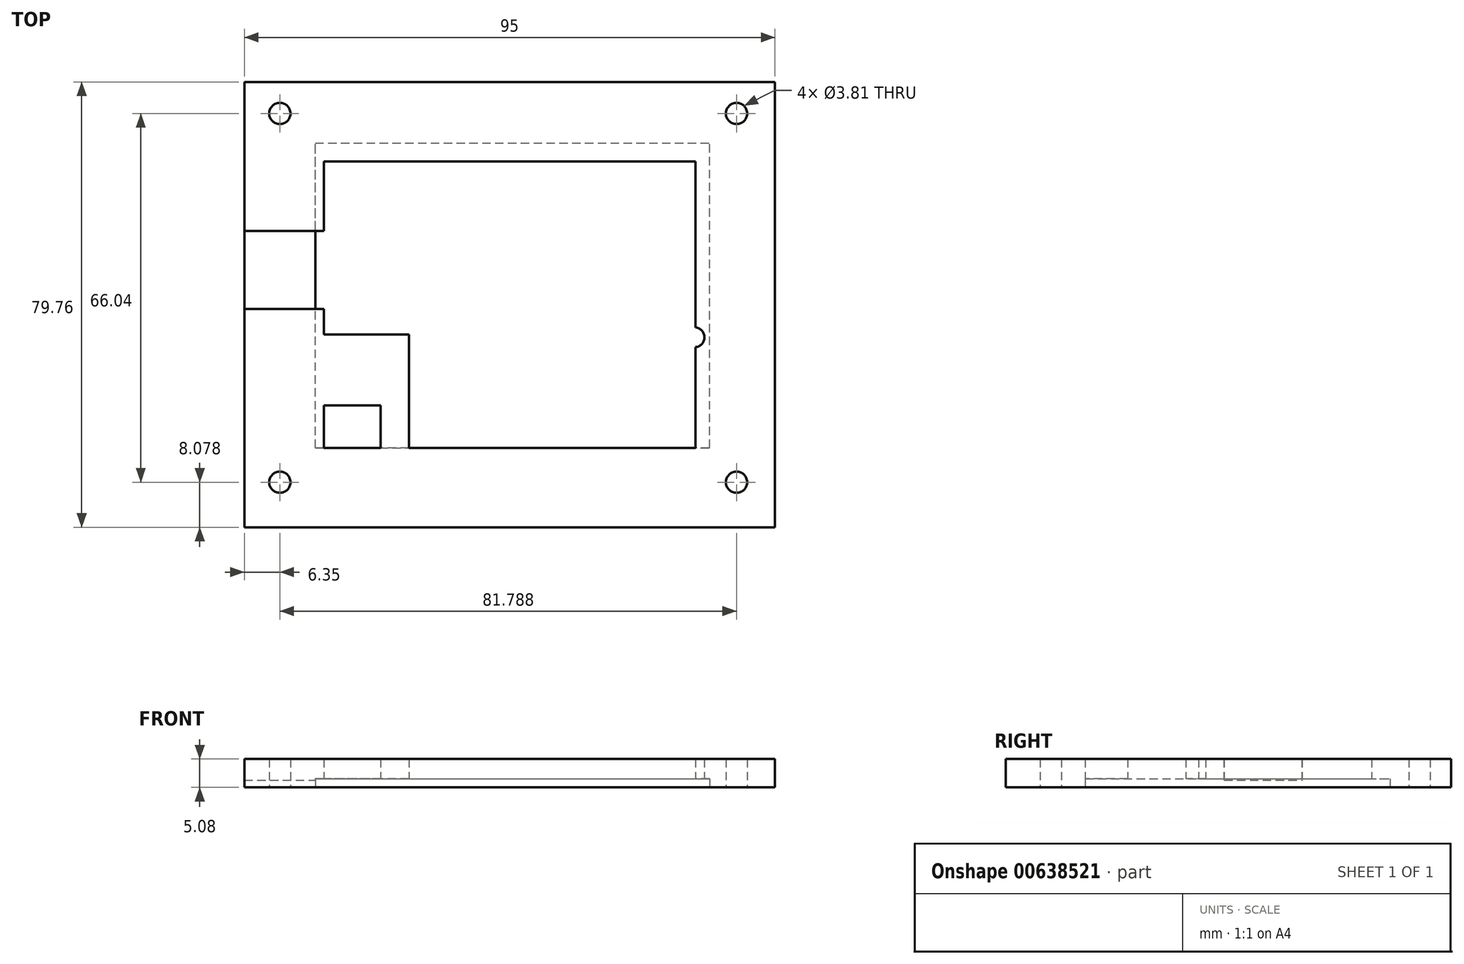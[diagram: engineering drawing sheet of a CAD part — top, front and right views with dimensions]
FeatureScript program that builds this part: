
annotation { "Feature Type Name" : "Feature", "Feature Type Description" : "" }
export const myFeature = defineFeature(function(context is Context, id is Id, definition is map)
    precondition{}
    {
        {
            var Q0;
            Q0=qCreatedBy(makeId("Top.planeOp"),FACE);
            var sketch = newSketch(context, id + "F0", { "sketchPlane" : qUnion([Q0])});
            skLineSegment(sketch, "E0.bottom", {"start": v(0, 0) * mm, "end": v(95, 0) * mm});
            skLineSegment(sketch, "E0.top", {"start": v(0, 79.76) * mm, "end": v(95, 79.76) * mm});
            skLineSegment(sketch, "E0.left", {"start": v(0, 0) * mm, "end": v(0, 79.76) * mm});
            skLineSegment(sketch, "E0.right", {"start": v(95, 0) * mm, "end": v(95, 79.76) * mm});
            skLineSegment(sketch, "E1.bottom", {"start": v(80.77, 65.53) * mm, "end": v(14.22, 65.53) * mm});
            skLineSegment(sketch, "E1.top", {"start": v(80.77, 14.22) * mm, "end": v(29.46, 14.22) * mm});
            skLineSegment(sketch, "E1.left", {"start": v(80.77, 65.53) * mm, "end": v(80.77, 14.22) * mm});
            skLineSegment(sketch, "E1.right", {"start": v(14.22, 65.53) * mm, "end": v(14.22, 34.54) * mm});
            skLineSegment(sketch, "E2.bottom", {"start": v(14.22, 14.22) * mm, "end": v(24.38, 14.22) * mm});
            skLineSegment(sketch, "E2.top", {"start": v(14.22, 21.84) * mm, "end": v(24.38, 21.84) * mm});
            skLineSegment(sketch, "E2.left", {"start": v(14.22, 14.22) * mm, "end": v(14.22, 21.84) * mm});
            skLineSegment(sketch, "E2.right", {"start": v(24.38, 14.22) * mm, "end": v(24.38, 21.84) * mm});
            skLineSegment(sketch, "E3", {"start": v(14.22, 34.54) * mm, "end": v(29.46, 34.54) * mm});
            skLineSegment(sketch, "E4", {"start": v(29.46, 34.54) * mm, "end": v(29.46, 14.22) * mm});
            skLineSegment(sketch, "E5.trimOffspring", {"start": v(24.38, 14.22) * mm, "end": v(14.22, 14.22) * mm});
            skSolve(sketch);
        }
        {
            var Q0;
            Q0 = qSketchRegion(id + "F0", true);
            extrude(context, id + "F1", {"entities" : qUnion([Q0]), "depth" : 5.08 * mm, "offsetDistance" : 25.4 * mm});
        }
        {
            var Q0;
            Q0=makeQuery(id+"F1.opExtrude","CAP_FACE",FACE,{"disambiguationData":[OSD([sQuery(id+"F0.wireOp",EDGE,"E0.bottom"),sQuery(id+"F0.wireOp",EDGE,"E0.top"),sQuery(id+"F0.wireOp",EDGE,"E0.left"),sQuery(id+"F0.wireOp",EDGE,"E0.right"),sQuery(id+"F0.wireOp",EDGE,"E1.bottom"),sQuery(id+"F0.wireOp",EDGE,"E1.top"),sQuery(id+"F0.wireOp",EDGE,"E1.left"),sQuery(id+"F0.wireOp",EDGE,"E1.right"),sQuery(id+"F0.wireOp",EDGE,"E2.top"),sQuery(id+"F0.wireOp",EDGE,"E2.left"),sQuery(id+"F0.wireOp",EDGE,"E2.right"),sQuery(id+"F0.wireOp",EDGE,"E3"),sQuery(id+"F0.wireOp",EDGE,"E4"),sQuery(id+"F0.wireOp",EDGE,"E5.trimOffspring")])],"isStart":true});
            var sketch = newSketch(context, id + "F2", { "sketchPlane" : qUnion([Q0])});
            skLineSegment(sketch, "E6.bottom", {"start": v(12.7, -14.22) * mm, "end": v(83.31, -14.22) * mm});
            skLineSegment(sketch, "E6.top", {"start": v(12.7, -68.83) * mm, "end": v(83.31, -68.83) * mm});
            skLineSegment(sketch, "E6.left", {"start": v(12.7, -14.22) * mm, "end": v(12.7, -68.83) * mm});
            skLineSegment(sketch, "E6.right", {"start": v(83.31, -14.22) * mm, "end": v(83.31, -68.83) * mm});
            skSolve(sketch);
        }
        {
            var Q0;
            Q0 = qSketchRegion(id + "F2", true);
            extrude(context, id + "F3", {"entities" : qUnion([Q0]), "operationType" : NewBodyOperationType.REMOVE, "oppositeDirection" : true, "depth" : 1.52 * mm, "offsetDistance" : 25.4 * mm});
        }
        {
            var Q0;
            Q0=makeQuery(id+"F3.boolean.opBoolean","COPY",FACE,{"derivedFrom":makeQuery(id+"F3.opExtrude","CAP_FACE",FACE,{"disambiguationData":[OSD([sQuery(id+"F2.wireOp",EDGE,"E6.bottom"),sQuery(id+"F2.wireOp",EDGE,"E6.top"),sQuery(id+"F2.wireOp",EDGE,"E6.left"),sQuery(id+"F2.wireOp",EDGE,"E6.right")])],"isStart":false})});
            var sketch = newSketch(context, id + "F4", { "sketchPlane" : qUnion([Q0])});
            skArc(sketch, "E7", {"start": v(80.77, -35.8) * mm, "mid": v(82.4, -34.03) * mm, "end": v(80.77, -32.26) * mm});
            skLineSegment(sketch, "E8", {"start": v(80.77, -32.26) * mm, "end": v(80.77, -35.8) * mm});
            skSolve(sketch);
        }
        {
            var Q0;
            Q0 = qSketchRegion(id + "F4", true);
            extrude(context, id + "F5", {"entities" : qUnion([Q0]), "operationType" : NewBodyOperationType.REMOVE, "oppositeDirection" : true, "depth" : 25.4 * mm, "offsetDistance" : 25.4 * mm});
        }
        {
            var Q0;
            Q0=makeQuery(id+"F1.opExtrude","CAP_FACE",FACE,{"disambiguationData":[OSD([sQuery(id+"F0.wireOp",EDGE,"E0.bottom"),sQuery(id+"F0.wireOp",EDGE,"E0.top"),sQuery(id+"F0.wireOp",EDGE,"E0.left"),sQuery(id+"F0.wireOp",EDGE,"E0.right"),sQuery(id+"F0.wireOp",EDGE,"E1.bottom"),sQuery(id+"F0.wireOp",EDGE,"E1.top"),sQuery(id+"F0.wireOp",EDGE,"E1.left"),sQuery(id+"F0.wireOp",EDGE,"E1.right"),sQuery(id+"F0.wireOp",EDGE,"E2.top"),sQuery(id+"F0.wireOp",EDGE,"E2.left"),sQuery(id+"F0.wireOp",EDGE,"E2.right"),sQuery(id+"F0.wireOp",EDGE,"E3"),sQuery(id+"F0.wireOp",EDGE,"E4"),sQuery(id+"F0.wireOp",EDGE,"E5.trimOffspring")])],"isStart":true});
            var sketch = newSketch(context, id + "F6", { "sketchPlane" : qUnion([Q0])});
            skCircle(sketch, "E9", {"center": v(6.35, -8.08) * mm, "radius": 1.9 * mm});
            skCircle(sketch, "E10.1.0.0", {"center": v(88.14, -8.08) * mm, "radius": 1.9 * mm});
            skLineSegment(sketch, "E10.direction1", {"start": v(6.35, -8.08) * mm, "end": v(88.14, -8.08) * mm, "construction": true});
            skCircle(sketch, "E11.0.1.0", {"center": v(6.35, -74.12) * mm, "radius": 1.9 * mm});
            skCircle(sketch, "E11.0.1.1", {"center": v(88.14, -74.12) * mm, "radius": 1.9 * mm});
            skLineSegment(sketch, "E11.direction1", {"start": v(6.35, -8.08) * mm, "end": v(-19.05, -8.08) * mm, "construction": true});
            skLineSegment(sketch, "E11.direction2", {"start": v(6.35, -8.08) * mm, "end": v(6.35, -74.12) * mm, "construction": true});
            skSolve(sketch);
        }
        {
            var Q0;
            Q0 = qSketchRegion(id + "F6", true);
            extrude(context, id + "F7", {"entities" : qUnion([Q0]), "operationType" : NewBodyOperationType.REMOVE, "oppositeDirection" : true, "depth" : 25.4 * mm, "offsetDistance" : 25.4 * mm});
        }
        {
            var Q0;
            Q0=makeQuery(id+"F1.opExtrude","CAP_FACE",FACE,{"disambiguationData":[OSD([sQuery(id+"F0.wireOp",EDGE,"E0.bottom"),sQuery(id+"F0.wireOp",EDGE,"E0.top"),sQuery(id+"F0.wireOp",EDGE,"E0.left"),sQuery(id+"F0.wireOp",EDGE,"E0.right"),sQuery(id+"F0.wireOp",EDGE,"E1.bottom"),sQuery(id+"F0.wireOp",EDGE,"E1.top"),sQuery(id+"F0.wireOp",EDGE,"E1.left"),sQuery(id+"F0.wireOp",EDGE,"E1.right"),sQuery(id+"F0.wireOp",EDGE,"E2.top"),sQuery(id+"F0.wireOp",EDGE,"E2.left"),sQuery(id+"F0.wireOp",EDGE,"E2.right"),sQuery(id+"F0.wireOp",EDGE,"E3"),sQuery(id+"F0.wireOp",EDGE,"E4"),sQuery(id+"F0.wireOp",EDGE,"E5.trimOffspring")])],"isStart":false});
            var sketch = newSketch(context, id + "F8", { "sketchPlane" : qUnion([Q0])});
            skLineSegment(sketch, "E12.bottom", {"start": v(-4, 39.12) * mm, "end": v(20.78, 39.12) * mm});
            skLineSegment(sketch, "E12.top", {"start": v(-4, 53.09) * mm, "end": v(20.78, 53.09) * mm});
            skLineSegment(sketch, "E12.left", {"start": v(-4, 39.12) * mm, "end": v(-4, 53.09) * mm});
            skLineSegment(sketch, "E12.right", {"start": v(20.78, 39.12) * mm, "end": v(20.78, 53.09) * mm});
            skSolve(sketch);
        }
        {
            var Q0;
            Q0 = qSketchRegion(id + "F8", true);
            extrude(context, id + "F9", {"entities" : qUnion([Q0]), "operationType" : NewBodyOperationType.REMOVE, "oppositeDirection" : true, "depth" : 3.8 * mm, "offsetDistance" : 25.4 * mm});
        }
    });
